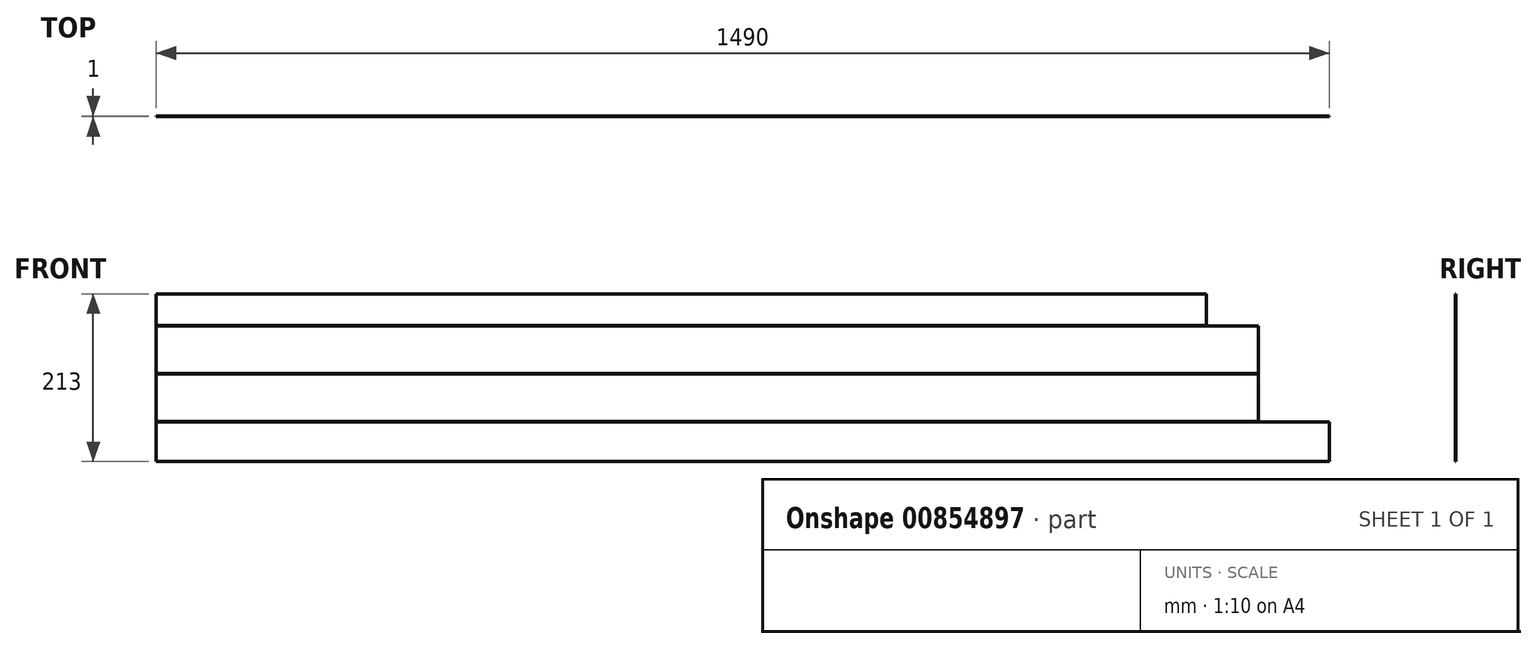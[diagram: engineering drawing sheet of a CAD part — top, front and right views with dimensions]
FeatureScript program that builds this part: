
annotation { "Feature Type Name" : "Feature", "Feature Type Description" : "" }
export const myFeature = defineFeature(function(context is Context, id is Id, definition is map)
    precondition{}
    {
        {
            var Q0;
            Q0=qCreatedBy(makeId("Front.planeOp"),FACE);
            var sketch = newSketch(context, id + "F0", { "sketchPlane" : qUnion([Q0])});
            skLineSegment(sketch, "E0", {"start": v(0, 0) * mm, "end": v(1490, 0) * mm});
            skLineSegment(sketch, "E1", {"start": v(1490, 0) * mm, "end": v(1490, 50) * mm});
            skLineSegment(sketch, "E2", {"start": v(1490, 50) * mm, "end": v(0, 50) * mm});
            skLineSegment(sketch, "E3", {"start": v(0, 50) * mm, "end": v(0, 0) * mm});
            skLineSegment(sketch, "E4", {"start": v(0, 50) * mm, "end": v(0, 111) * mm});
            skLineSegment(sketch, "E5", {"start": v(0, 111) * mm, "end": v(1400, 111) * mm});
            skLineSegment(sketch, "E6", {"start": v(1400, 111) * mm, "end": v(1400, 50) * mm});
            skLineSegment(sketch, "E7", {"start": v(1400, 50) * mm, "end": v(0, 50) * mm});
            skLineSegment(sketch, "E8", {"start": v(0, 111) * mm, "end": v(0, 172) * mm});
            skLineSegment(sketch, "E9", {"start": v(0, 172) * mm, "end": v(1400, 172) * mm});
            skLineSegment(sketch, "E10", {"start": v(1400, 172) * mm, "end": v(1400, 111) * mm});
            skLineSegment(sketch, "E11", {"start": v(0, 172) * mm, "end": v(0, 213) * mm});
            skLineSegment(sketch, "E12", {"start": v(0, 213) * mm, "end": v(1333.98, 213) * mm});
            skLineSegment(sketch, "E13", {"start": v(1333.98, 213) * mm, "end": v(1333.98, 172) * mm});
            skLineSegment(sketch, "E14", {"start": v(1333.98, 172) * mm, "end": v(0, 172) * mm});
            skLineSegment(sketch, "E15", {"start": v(0, 50) * mm, "end": v(0, 51) * mm});
            skLineSegment(sketch, "E16", {"start": v(0, 51) * mm, "end": v(1400, 51) * mm});
            skLineSegment(sketch, "E17", {"start": v(1400, 51) * mm, "end": v(1400, 50) * mm});
            skLineSegment(sketch, "E18", {"start": v(0, 111) * mm, "end": v(0, 112) * mm});
            skLineSegment(sketch, "E19", {"start": v(0, 112) * mm, "end": v(1400, 112) * mm});
            skLineSegment(sketch, "E20", {"start": v(1400, 112) * mm, "end": v(1400, 111) * mm});
            skLineSegment(sketch, "E21", {"start": v(0, 172) * mm, "end": v(0, 173) * mm});
            skLineSegment(sketch, "E22", {"start": v(0, 173) * mm, "end": v(1333.98, 173) * mm});
            skLineSegment(sketch, "E23", {"start": v(1333.98, 173) * mm, "end": v(1333.98, 172) * mm});
            skSolve(sketch);
        }
        {
            var Q0;
            {var subQ2=sQuery(id+"F0.wireOp",EDGE,"E12");Q0=makeQuery(id+"F0.imprint","IMPRINT",FACE,{"disambiguationData":[TD([[makeQuery(id+"F0.imprint","IMPRINT",EDGE,{"derivedFrom":subQ2}),-1.0]])]});}
            var Q1;
            {var subQ3=sQuery(id+"F0.wireOp",EDGE,"E19");Q1=makeQuery(id+"F0.imprint","IMPRINT",FACE,{"disambiguationData":[TD([[makeQuery(id+"F0.imprint","IMPRINT",EDGE,{"derivedFrom":subQ3}),1.0]])]});}
            var Q2;
            {var subQ2=sQuery(id+"F0.wireOp",EDGE,"E5");Q2=makeQuery(id+"F0.imprint","IMPRINT",FACE,{"disambiguationData":[TD([[makeQuery(id+"F0.imprint","IMPRINT",EDGE,{"derivedFrom":subQ2}),-1.0]])]});}
            var Q3;
            Q3=makeQuery(id+"F0.imprint","IMPRINT",FACE,{"disambiguationData":[TD([[makeQuery(id+"F0.imprint","IMPRINT",EDGE,{"derivedFrom":sQuery(id+"F0.wireOp",EDGE,"E0")}),1.0]])]});
            extrude(context, id + "F1", {"entities" : qUnion([Q0, Q1, Q2, Q3]), "depth" : 1 * mm, "offsetDistance" : 25 * mm});
        }
    });
